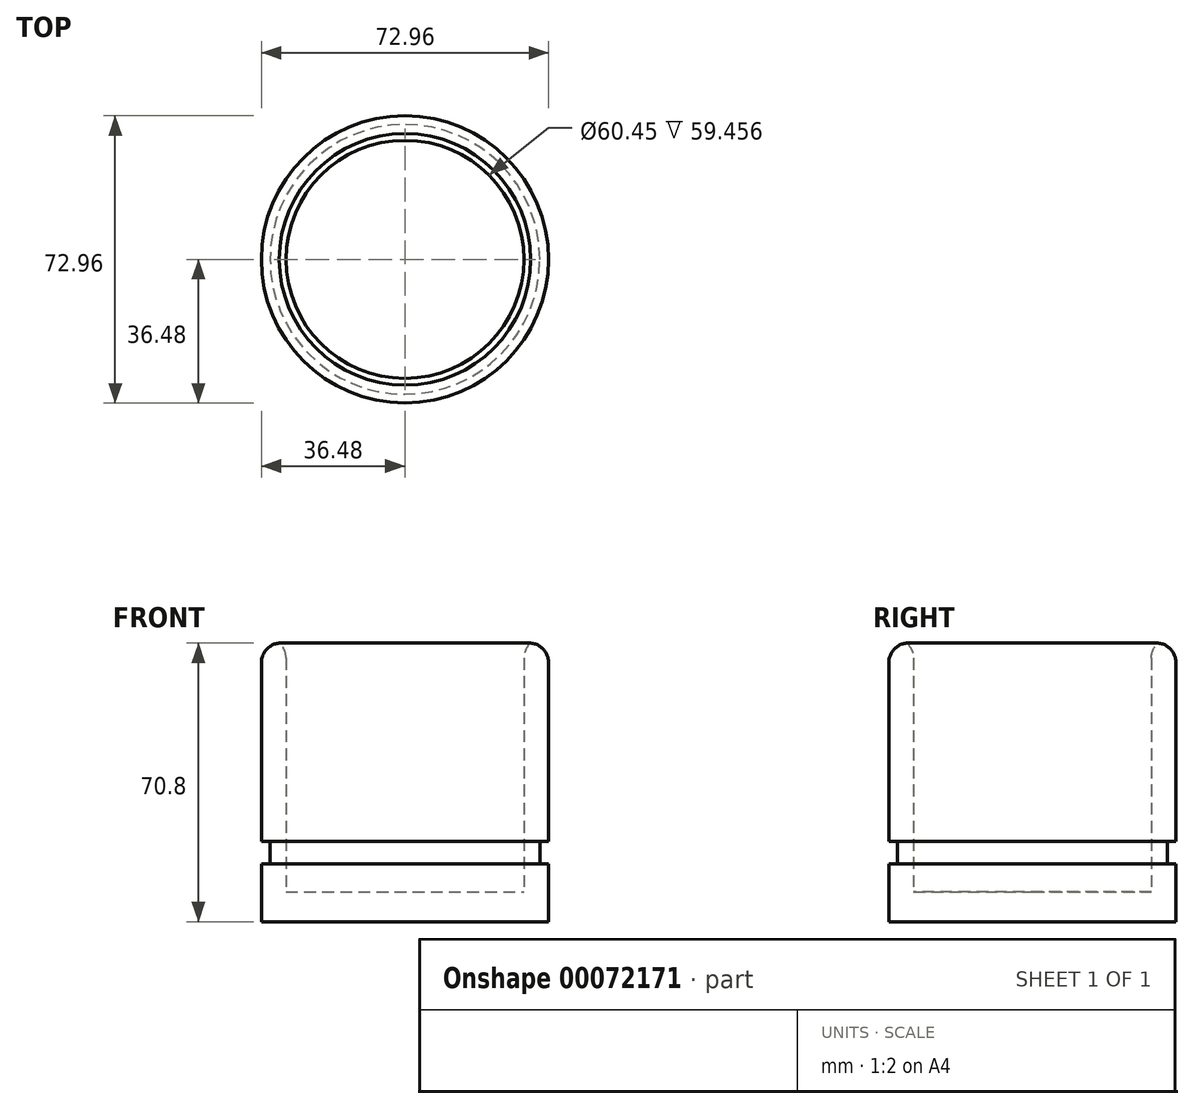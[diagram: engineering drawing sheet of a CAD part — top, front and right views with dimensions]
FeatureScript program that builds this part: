
annotation { "Feature Type Name" : "Feature", "Feature Type Description" : "" }
export const myFeature = defineFeature(function(context is Context, id is Id, definition is map)
    precondition{}
    {
        {
            var Q0;
            Q0=qCreatedBy(makeId("Front.planeOp"),FACE);
            var sketch = newSketch(context, id + "F0", { "sketchPlane" : qUnion([Q0])});
            skLineSegment(sketch, "E0", {"start": v(-36.48, 36.5) * mm, "end": v(-36.48, -13.5) * mm});
            skLineSegment(sketch, "E1", {"start": v(-36.48, -13.5) * mm, "end": v(-34.26, -13.5) * mm});
            skLineSegment(sketch, "E2", {"start": v(-34.26, -13.5) * mm, "end": v(-34.26, -19.22) * mm});
            skLineSegment(sketch, "E3", {"start": v(-34.26, -19.22) * mm, "end": v(-36.48, -19.22) * mm});
            skLineSegment(sketch, "E4", {"start": v(-36.48, -19.22) * mm, "end": v(-36.48, -33.87) * mm});
            skLineSegment(sketch, "E5", {"start": v(-36.48, -33.87) * mm, "end": v(-19.91, -33.87) * mm});
            skLineSegment(sketch, "E6", {"start": v(-19.91, -33.87) * mm, "end": v(0, -33.87) * mm});
            skLineSegment(sketch, "E7", {"start": v(0, -33.87) * mm, "end": v(0, -26.3) * mm});
            skLineSegment(sketch, "E8", {"start": v(0, -26.3) * mm, "end": v(-30.22, -26.3) * mm});
            skLineSegment(sketch, "E9", {"start": v(-30.22, -26.3) * mm, "end": v(-30.22, 37.09) * mm});
            skLineSegment(sketch, "E10", {"start": v(-30.22, 37.09) * mm, "end": v(-36.48, 36.5) * mm});
            skSolve(sketch);
        }
        {
            var Q0;
            Q0=makeQuery(id+"F0.imprint","IMPRINT",FACE,{"disambiguationData":[TD([[makeQuery(id+"F0.imprint","IMPRINT",EDGE,{"derivedFrom":sQuery(id+"F0.wireOp",EDGE,"E0")}),1.0]])]});
            var Q1;
            Q1=sQuery(id+"F0.wireOp",EDGE,"E7");
            revolve(context, id + "F1", {"entities" : qUnion([Q0]), "axis" : qUnion([Q1]), "revolveType" : RevolveType.FULL});
        }
        {
            var Q0;
            Q0=makeQuery(id+"F1.opRevolve","SWEPT_EDGE",EDGE,{"disambiguationData":[OSD([sQuery(id+"F0.wireOp",EDGE,"E0"),sQuery(id+"F0.wireOp",EDGE,"E10")])]});
            fillet(context, id + "F2", {"entities" : qUnion([Q0]), "radius" : 5 * mm, "tangentPropagation" : true, "allowEdgeOverflow" : false});
        }
        {
            var Q0;
            {var subQ0=sQuery(id+"F0.wireOp",EDGE,"E10");Q0=makeQuery(id+"F2.opFillet","BLEND_EDGE",EDGE,{"blendedFrom":[makeQuery(id+"F1.opRevolve","SWEPT_EDGE",EDGE,{"disambiguationData":[OSD([sQuery(id+"F0.wireOp",EDGE,"E0"),subQ0])]}),makeQuery(id+"F1.opRevolve","SWEPT_FACE",FACE,{"disambiguationData":[OSD([subQ0])]})],"blendedInto":[makeQuery(id+"F1.opRevolve","SWEPT_FACE",FACE,{"disambiguationData":[OSD([subQ0])]})]});}
            var Q1;
            Q1=makeQuery(id+"F1.opRevolve","SWEPT_EDGE",EDGE,{"disambiguationData":[OSD([sQuery(id+"F0.wireOp",EDGE,"E9"),sQuery(id+"F0.wireOp",EDGE,"E10")])]});
            fillet(context, id + "F3", {"entities" : qUnion([Q0, Q1]), "radius" : 5 * mm, "tangentPropagation" : true, "allowEdgeOverflow" : false});
        }
    });
